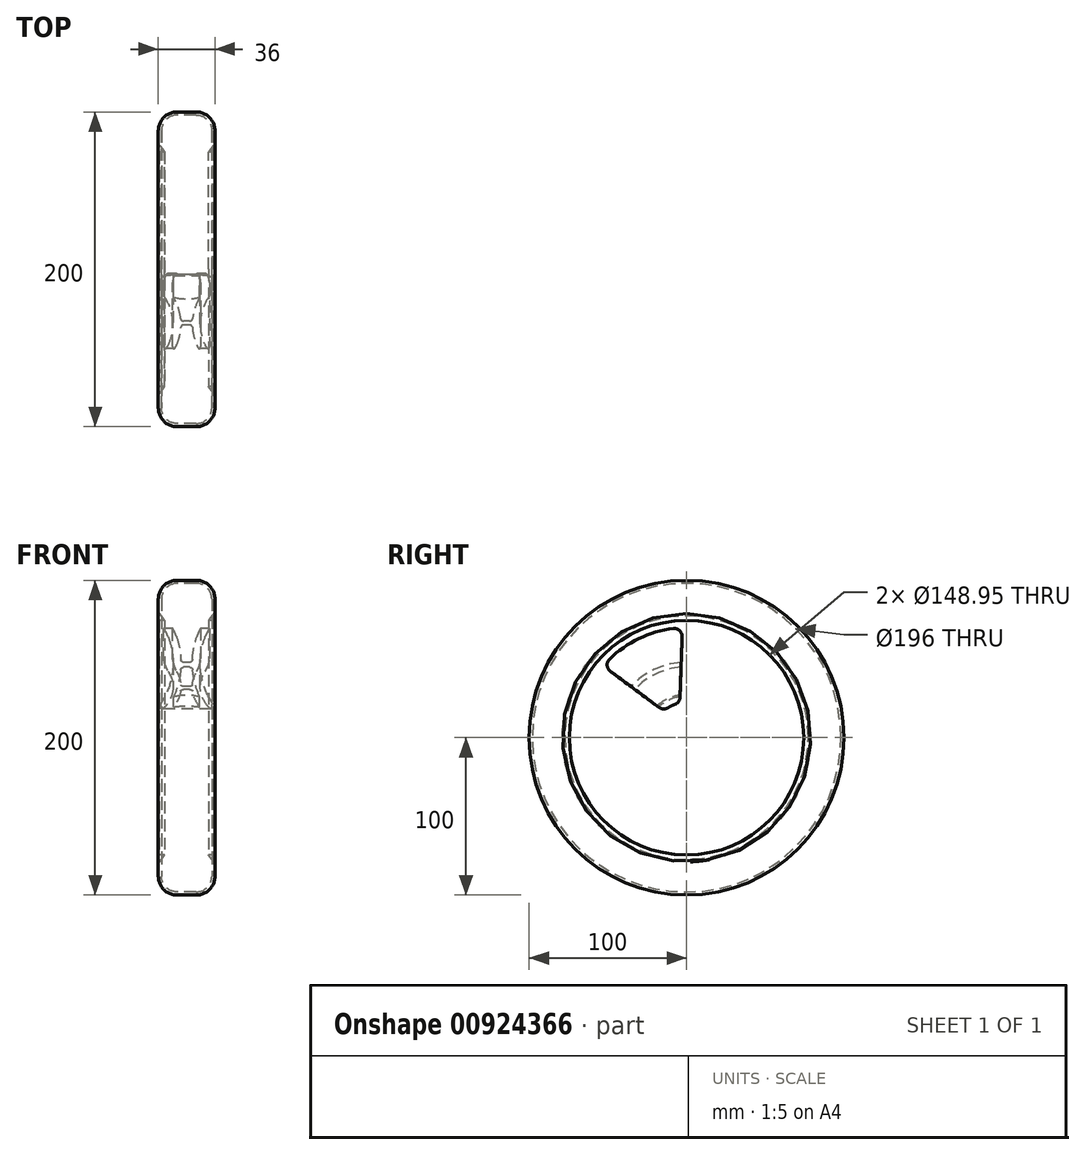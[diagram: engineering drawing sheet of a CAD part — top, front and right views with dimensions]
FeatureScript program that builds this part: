
annotation { "Feature Type Name" : "Feature", "Feature Type Description" : "" }
export const myFeature = defineFeature(function(context is Context, id is Id, definition is map)
    precondition{}
    {
        {
            var Q0;
            Q0=qCreatedBy(makeId("Front.planeOp"),FACE);
            var sketch = newSketch(context, id + "F0", { "sketchPlane" : qUnion([Q0])});
            skLineSegment(sketch, "E0", {"start": v(0, 0) * mm, "end": v(0, 100) * mm, "construction": true});
            skLineSegment(sketch, "E1", {"start": v(0, 10) * mm, "end": v(-18, 10) * mm});
            skLineSegment(sketch, "E2", {"start": v(-18, 10) * mm, "end": v(-18, 16.78) * mm});
            skLineSegment(sketch, "E3", {"start": v(0, 100) * mm, "end": v(-6, 100) * mm});
            skLineSegment(sketch, "E4", {"start": v(-18, 88) * mm, "end": v(-18, 79.22) * mm});
            skArc(sketch, "E5", {"start": v(-16.3, 22.36) * mm, "mid": v(-8.63, 48.63) * mm, "end": v(-17.6, 74.48) * mm});
            skArc(sketch, "E6.0", {"start": v(-13.48, 73.83) * mm, "mid": v(-15.23, 76.3) * mm, "end": v(-17.12, 78.67) * mm});
            skPoint(sketch, "E7.orphan", {"position": v(0, 75) * mm});
            skArc(sketch, "E8.MirrorCS", {"start": v(13.48, 73.83) * mm, "mid": v(15.23, 76.3) * mm, "end": v(17.12, 78.67) * mm});
            skArc(sketch, "E9.MirrorCS", {"start": v(16.3, 22.36) * mm, "mid": v(8.63, 48.63) * mm, "end": v(17.6, 74.48) * mm});
            skLineSegment(sketch, "E10.MirrorCS", {"start": v(18, 78.35) * mm, "end": v(18, 75.67) * mm});
            skLineSegment(sketch, "E11.MirrorCS", {"start": v(0, 100) * mm, "end": v(6, 100) * mm});
            skLineSegment(sketch, "E12.MirrorCS", {"start": v(0, 10) * mm, "end": v(18, 10) * mm});
            skLineSegment(sketch, "E13.MirrorCS", {"start": v(18, 10) * mm, "end": v(18, 16.78) * mm});
            skArc(sketch, "E14", {"start": v(-13.48, 73.83) * mm, "mid": v(0, 72.36) * mm, "end": v(13.48, 73.83) * mm});
            skPoint(sketch, "E15.orphan", {"position": v(-14.28, 20) * mm});
            skPoint(sketch, "E16.orphan", {"position": v(14.28, 20) * mm});
            skPoint(sketch, "E17.visualSharp", {"position": v(-18, 100) * mm});
            skArc(sketch, "E17.filletArc", {"start": v(-6, 100) * mm, "mid": v(-14.49, 96.49) * mm, "end": v(-18, 88) * mm});
            skArc(sketch, "E18.MirrorCS", {"start": v(6, 100) * mm, "mid": v(14.49, 96.49) * mm, "end": v(18, 88) * mm});
            skPoint(sketch, "E19.orphan", {"position": v(18, 100) * mm});
            skLineSegment(sketch, "E20", {"start": v(-18, 78.35) * mm, "end": v(-18, 75.67) * mm});
            skPoint(sketch, "E21.visualSharp", {"position": v(-18, 79.68) * mm});
            skArc(sketch, "E21.filletArc", {"start": v(-17.12, 78.67) * mm, "mid": v(-17.67, 78.82) * mm, "end": v(-18, 78.35) * mm});
            skPoint(sketch, "E22.newPointA", {"position": v(18, 79.68) * mm});
            skArc(sketch, "E22.filletArc", {"start": v(18, 78.35) * mm, "mid": v(17.67, 78.82) * mm, "end": v(17.12, 78.67) * mm});
            skLineSegment(sketch, "E23.MirrorCS", {"start": v(18, 88) * mm, "end": v(18, 79.22) * mm});
            skPoint(sketch, "E24.1.start.orphan", {"position": v(-6, 97) * mm});
            skPoint(sketch, "E25.0.start.orphan", {"position": v(0, 97) * mm});
            skPoint(sketch, "E26.MirrorCS.end.orphan", {"position": v(6, 97) * mm});
            skPoint(sketch, "E27.MirrorCS.end.orphan", {"position": v(15, 88) * mm});
            skPoint(sketch, "E28.MirrorCS.end.orphan", {"position": v(15, 80.8) * mm});
            skPoint(sketch, "E29.MirrorCS.start.orphan", {"position": v(9.5, 73.08) * mm});
            skPoint(sketch, "E30.0.start.orphan", {"position": v(-9.5, 73.08) * mm});
            skPoint(sketch, "E24.0.end.orphan", {"position": v(-15, 80.8) * mm});
            skPoint(sketch, "E24.0.start.orphan", {"position": v(-15, 88) * mm});
            skPoint(sketch, "E31.visualSharp", {"position": v(-18, 75) * mm});
            skArc(sketch, "E31.filletArc", {"start": v(-18, 75.67) * mm, "mid": v(-17.9, 75.04) * mm, "end": v(-17.6, 74.48) * mm});
            skPoint(sketch, "E32.visualSharp", {"position": v(18, 75) * mm});
            skArc(sketch, "E32.filletArc", {"start": v(17.6, 74.48) * mm, "mid": v(17.9, 75.04) * mm, "end": v(18, 75.67) * mm});
            skLineSegment(sketch, "E33.0", {"start": v(-16, 88) * mm, "end": v(-16, 77.31) * mm});
            skArc(sketch, "E33.1", {"start": v(-6, 98) * mm, "mid": v(-13.07, 95.07) * mm, "end": v(-16, 88) * mm});
            skLineSegment(sketch, "E33.2", {"start": v(16, 88) * mm, "end": v(16, 77.31) * mm});
            skArc(sketch, "E33.3", {"start": v(6, 98) * mm, "mid": v(13.07, 95.07) * mm, "end": v(16, 88) * mm});
            skLineSegment(sketch, "E33.4", {"start": v(0, 98) * mm, "end": v(6, 98) * mm});
            skLineSegment(sketch, "E33.5", {"start": v(0, 98) * mm, "end": v(-6, 98) * mm});
            skPoint(sketch, "E34.visualSharp", {"position": v(-18, 78.35) * mm});
            skArc(sketch, "E34.filletArc", {"start": v(-18, 79.22) * mm, "mid": v(-17.87, 78.93) * mm, "end": v(-17.57, 78.84) * mm});
            skArc(sketch, "E35.MirrorCS", {"start": v(18, 79.22) * mm, "mid": v(17.87, 78.93) * mm, "end": v(17.57, 78.84) * mm});
            skPoint(sketch, "E36.visualSharp", {"position": v(-18, 20) * mm});
            skArc(sketch, "E36.filletArc", {"start": v(-16.3, 22.36) * mm, "mid": v(-17.56, 19.7) * mm, "end": v(-18, 16.78) * mm});
            skPoint(sketch, "E37.visualSharp", {"position": v(18, 20) * mm});
            skArc(sketch, "E37.filletArc", {"start": v(18, 16.78) * mm, "mid": v(17.56, 19.7) * mm, "end": v(16.3, 22.36) * mm});
            skLineSegment(sketch, "E38", {"start": v(0, 0) * mm, "end": v(25.5, 0) * mm, "construction": true});
            skArc(sketch, "E39", {"start": v(8.32, 26.33) * mm, "mid": v(0, 27.6) * mm, "end": v(-8.32, 26.33) * mm});
            skArc(sketch, "E40.0", {"start": v(-8.32, 26.33) * mm, "mid": v(-5.33, 34.52) * mm, "end": v(-3.81, 43.1) * mm});
            skArc(sketch, "E40.2", {"start": v(8.32, 26.33) * mm, "mid": v(5.33, 34.52) * mm, "end": v(3.81, 43.1) * mm});
            skLineSegment(sketch, "E41", {"start": v(-3.63, 46.43) * mm, "end": v(3.63, 46.43) * mm, "construction": true});
            skLineSegment(sketch, "E42", {"start": v(-1.68, 47.93) * mm, "end": v(1.68, 47.93) * mm});
            skLineSegment(sketch, "E43.MirrorCS", {"start": v(-1.82, 44.93) * mm, "end": v(1.82, 44.93) * mm});
            skPoint(sketch, "E44.orphan", {"position": v(3.62, 44.93) * mm});
            skPoint(sketch, "E45.orphan", {"position": v(-3.62, 44.93) * mm});
            skArc(sketch, "E46.trimOffspring", {"start": v(3.67, 49.84) * mm, "mid": v(5.41, 60.78) * mm, "end": v(9.52, 71.06) * mm});
            skArc(sketch, "E47.trimOffspring", {"start": v(-3.67, 49.84) * mm, "mid": v(-5.41, 60.78) * mm, "end": v(-9.52, 71.06) * mm});
            skPoint(sketch, "E48.visualSharp", {"position": v(-3.62, 47.93) * mm});
            skArc(sketch, "E48.filletArc", {"start": v(-3.67, 49.84) * mm, "mid": v(-3.06, 48.49) * mm, "end": v(-1.68, 47.93) * mm});
            skPoint(sketch, "E49.visualSharp", {"position": v(3.62, 47.93) * mm});
            skArc(sketch, "E49.filletArc", {"start": v(1.68, 47.93) * mm, "mid": v(3.06, 48.49) * mm, "end": v(3.67, 49.84) * mm});
            skPoint(sketch, "E50.visualSharp", {"position": v(-3.69, 44.93) * mm});
            skArc(sketch, "E50.filletArc", {"start": v(-1.82, 44.93) * mm, "mid": v(-3.17, 44.4) * mm, "end": v(-3.81, 43.1) * mm});
            skPoint(sketch, "E51.visualSharp", {"position": v(3.69, 44.93) * mm});
            skArc(sketch, "E51.filletArc", {"start": v(3.81, 43.1) * mm, "mid": v(3.17, 44.4) * mm, "end": v(1.82, 44.93) * mm});
            skArc(sketch, "E52.0", {"start": v(-9.52, 71.06) * mm, "mid": v(0, 70.36) * mm, "end": v(9.52, 71.06) * mm});
            skSolve(sketch);
        }
        {
            var Q0;
            Q0=makeQuery(id+"F0.imprint","IMPRINT",FACE,{"disambiguationData":[TD([[makeQuery(id+"F0.imprint","IMPRINT",EDGE,{"derivedFrom":sQuery(id+"F0.wireOp",EDGE,"E1")}),-1.0]])]});
            var Q1;
            Q1=sQuery(id+"F0.wireOp",EDGE,"E38");
            revolve(context, id + "F1", {"surfaceOperationType" : NewSurfaceOperationType.NEW, "entities" : qUnion([Q0]), "axis" : qUnion([Q1]), "revolveType" : RevolveType.FULL});
        }
        {
            var Q0;
            Q0=makeQuery(id+"F0.imprint","IMPRINT",FACE,{"disambiguationData":[TD([[makeQuery(id+"F0.imprint","IMPRINT",EDGE,{"derivedFrom":sQuery(id+"F0.wireOp",EDGE,"E3")}),1.0]])]});
            var Q1;
            Q1=sQuery(id+"F0.wireOp",EDGE,"E38");
            revolve(context, id + "F2", {"surfaceOperationType" : NewSurfaceOperationType.NEW, "entities" : qUnion([Q0]), "axis" : qUnion([Q1]), "revolveType" : RevolveType.FULL});
        }
        {
            var Q0;
            Q0=qCreatedBy(makeId("Right.planeOp"),FACE);
            var sketch = newSketch(context, id + "F3", { "sketchPlane" : qUnion([Q0])});
            skArc(sketch, "E53.0", {"start": v(-11.82, 18.99) * mm, "mid": v(-9.7, 20.15) * mm, "end": v(-7.48, 21.08) * mm});
            skCircle(sketch, "E54.0", {"center": v(0, 0) * mm, "radius": 74.48 * mm});
            skPoint(sketch, "E55.0", {"position": v(0, 72.36) * mm});
            skLineSegment(sketch, "E56", {"start": v(0, 69.82) * mm, "end": v(0, 22.36) * mm, "construction": true});
            skArc(sketch, "E57", {"start": v(48.95, 49.79) * mm, "mid": v(30.3, 62.9) * mm, "end": v(8.4, 69.31) * mm});
            skLineSegment(sketch, "E58", {"start": v(2.8, 64.17) * mm, "end": v(4.15, 25.61) * mm});
            skLineSegment(sketch, "E59.MirrorCS", {"start": v(-2.8, 64.17) * mm, "end": v(-4.15, 25.61) * mm});
            skLineSegment(sketch, "E60.1.0", {"start": v(-51.92, 37.82) * mm, "end": v(-22.62, 12.72) * mm});
            skLineSegment(sketch, "E60.1.1", {"start": v(-48.42, 42.2) * mm, "end": v(-17.44, 19.22) * mm});
            skLineSegment(sketch, "E60.2.0", {"start": v(-61.94, -17.02) * mm, "end": v(-24.05, -9.75) * mm});
            skLineSegment(sketch, "E60.2.1", {"start": v(-63.19, -11.54) * mm, "end": v(-25.9, -1.65) * mm});
            skLineSegment(sketch, "E60.3.0", {"start": v(-25.31, -59.04) * mm, "end": v(-7.37, -24.88) * mm});
            skLineSegment(sketch, "E60.3.1", {"start": v(-30.37, -56.6) * mm, "end": v(-14.86, -21.28) * mm});
            skLineSegment(sketch, "E60.4.0", {"start": v(30.37, -56.6) * mm, "end": v(14.86, -21.28) * mm});
            skLineSegment(sketch, "E60.4.1", {"start": v(25.31, -59.04) * mm, "end": v(7.37, -24.88) * mm});
            skLineSegment(sketch, "E60.5.0", {"start": v(63.19, -11.54) * mm, "end": v(25.9, -1.65) * mm});
            skLineSegment(sketch, "E60.5.1", {"start": v(61.94, -17.02) * mm, "end": v(24.05, -9.75) * mm});
            skLineSegment(sketch, "E60.6.0", {"start": v(48.42, 42.2) * mm, "end": v(17.44, 19.22) * mm});
            skLineSegment(sketch, "E60.6.1", {"start": v(51.92, 37.82) * mm, "end": v(22.62, 12.72) * mm});
            skArc(sketch, "E61.trimOffspring", {"start": v(-8.4, 69.31) * mm, "mid": v(-30.3, 62.9) * mm, "end": v(-48.95, 49.79) * mm});
            skArc(sketch, "E62.trimOffspring", {"start": v(-59.43, 36.64) * mm, "mid": v(-68.07, 15.54) * mm, "end": v(-69.44, -7.23) * mm});
            skArc(sketch, "E63.trimOffspring", {"start": v(7.48, 21.08) * mm, "mid": v(9.7, 20.15) * mm, "end": v(11.82, 18.99) * mm});
            skArc(sketch, "E64.trimOffspring", {"start": v(18.88, -11.98) * mm, "mid": v(17.48, -13.94) * mm, "end": v(15.88, -15.74) * mm});
            skArc(sketch, "E65.trimOffspring", {"start": v(-15.88, -15.74) * mm, "mid": v(-17.48, -13.94) * mm, "end": v(-18.88, -11.98) * mm});
            skArc(sketch, "E66.trimOffspring", {"start": v(2.4, -22.23) * mm, "mid": v(0, -22.36) * mm, "end": v(-2.4, -22.23) * mm});
            skArc(sketch, "E67.trimOffspring", {"start": v(-22.21, 2.6) * mm, "mid": v(-21.8, 4.98) * mm, "end": v(-21.14, 7.3) * mm});
            skArc(sketch, "E68.trimOffspring", {"start": v(-22.5, -66.1) * mm, "mid": v(0, -69.82) * mm, "end": v(22.5, -66.1) * mm});
            skArc(sketch, "E69.trimOffspring", {"start": v(37.65, -58.8) * mm, "mid": v(54.59, -43.53) * mm, "end": v(65.7, -23.62) * mm});
            skArc(sketch, "E70.trimOffspring", {"start": v(69.44, -7.23) * mm, "mid": v(68.07, 15.54) * mm, "end": v(59.43, 36.64) * mm});
            skArc(sketch, "E71.MirrorCS", {"start": v(22.21, 2.6) * mm, "mid": v(21.8, 4.98) * mm, "end": v(21.14, 7.3) * mm});
            skPoint(sketch, "E72.visualSharp", {"position": v(-52.92, 45.54) * mm});
            skArc(sketch, "E72.filletArc", {"start": v(-48.95, 49.79) * mm, "mid": v(-50.43, 45.87) * mm, "end": v(-48.42, 42.2) * mm});
            skArc(sketch, "E73.trimOffspring", {"start": v(-65.7, -23.62) * mm, "mid": v(-54.59, -43.53) * mm, "end": v(-37.65, -58.8) * mm});
            skPoint(sketch, "E74.visualSharp", {"position": v(-2.61, 69.77) * mm});
            skArc(sketch, "E74.filletArc", {"start": v(-2.8, 64.17) * mm, "mid": v(-4.42, 68.03) * mm, "end": v(-8.4, 69.31) * mm});
            skPoint(sketch, "E75.visualSharp", {"position": v(2.61, 69.77) * mm});
            skArc(sketch, "E75.filletArc", {"start": v(8.4, 69.31) * mm, "mid": v(4.42, 68.03) * mm, "end": v(2.8, 64.17) * mm});
            skPoint(sketch, "E76.visualSharp", {"position": v(52.92, 45.54) * mm});
            skArc(sketch, "E76.filletArc", {"start": v(48.42, 42.2) * mm, "mid": v(50.43, 45.87) * mm, "end": v(48.95, 49.79) * mm});
            skPoint(sketch, "E77.visualSharp", {"position": v(67.44, -18.07) * mm});
            skArc(sketch, "E77.filletArc", {"start": v(65.7, -23.62) * mm, "mid": v(65.34, -19.45) * mm, "end": v(61.94, -17.02) * mm});
            skPoint(sketch, "E78.visualSharp", {"position": v(32.62, -61.73) * mm});
            skArc(sketch, "E78.filletArc", {"start": v(30.37, -56.6) * mm, "mid": v(33.5, -59.38) * mm, "end": v(37.65, -58.8) * mm});
            skPoint(sketch, "E79.visualSharp", {"position": v(-27.92, -64) * mm});
            skArc(sketch, "E79.filletArc", {"start": v(-25.31, -59.04) * mm, "mid": v(-25.53, -63.21) * mm, "end": v(-22.5, -66.1) * mm});
            skPoint(sketch, "E80.visualSharp", {"position": v(-67.44, -18.07) * mm});
            skArc(sketch, "E80.filletArc", {"start": v(-61.94, -17.02) * mm, "mid": v(-65.34, -19.45) * mm, "end": v(-65.7, -23.62) * mm});
            skPoint(sketch, "E81.visualSharp", {"position": v(-56.18, 41.46) * mm});
            skArc(sketch, "E81.filletArc", {"start": v(-51.92, 37.82) * mm, "mid": v(-55.95, 38.96) * mm, "end": v(-59.43, 36.64) * mm});
            skPoint(sketch, "E82.visualSharp", {"position": v(-68.6, -12.98) * mm});
            skArc(sketch, "E82.filletArc", {"start": v(-69.44, -7.23) * mm, "mid": v(-67.3, -10.83) * mm, "end": v(-63.19, -11.54) * mm});
            skPoint(sketch, "E83.visualSharp", {"position": v(-32.62, -61.73) * mm});
            skArc(sketch, "E83.filletArc", {"start": v(-37.65, -58.8) * mm, "mid": v(-33.5, -59.38) * mm, "end": v(-30.37, -56.6) * mm});
            skPoint(sketch, "E84.visualSharp", {"position": v(27.92, -64) * mm});
            skArc(sketch, "E84.filletArc", {"start": v(22.5, -66.1) * mm, "mid": v(25.53, -63.21) * mm, "end": v(25.31, -59.04) * mm});
            skPoint(sketch, "E85.visualSharp", {"position": v(68.6, -12.98) * mm});
            skArc(sketch, "E85.filletArc", {"start": v(63.19, -11.54) * mm, "mid": v(67.3, -10.83) * mm, "end": v(69.44, -7.23) * mm});
            skPoint(sketch, "E86.visualSharp", {"position": v(56.18, 41.46) * mm});
            skArc(sketch, "E86.filletArc", {"start": v(59.43, 36.64) * mm, "mid": v(55.95, 38.96) * mm, "end": v(51.92, 37.82) * mm});
            skPoint(sketch, "E87.visualSharp", {"position": v(-14.5, 17.03) * mm});
            skArc(sketch, "E87.filletArc", {"start": v(-17.44, 19.22) * mm, "mid": v(-14.66, 18.24) * mm, "end": v(-11.82, 18.99) * mm});
            skPoint(sketch, "E88.visualSharp", {"position": v(-4.28, 21.95) * mm});
            skArc(sketch, "E88.filletArc", {"start": v(-7.48, 21.08) * mm, "mid": v(-5.12, 22.83) * mm, "end": v(-4.15, 25.61) * mm});
            skPoint(sketch, "E89.visualSharp", {"position": v(14.5, 17.03) * mm});
            skArc(sketch, "E89.filletArc", {"start": v(11.82, 18.99) * mm, "mid": v(14.66, 18.24) * mm, "end": v(17.44, 19.22) * mm});
            skPoint(sketch, "E90.visualSharp", {"position": v(22.35, -0.71) * mm});
            skArc(sketch, "E90.filletArc", {"start": v(22.21, 2.6) * mm, "mid": v(23.4, -0.1) * mm, "end": v(25.9, -1.65) * mm});
            skPoint(sketch, "E91.visualSharp", {"position": v(13.38, -17.92) * mm});
            skArc(sketch, "E91.filletArc", {"start": v(15.88, -15.74) * mm, "mid": v(14.52, -18.35) * mm, "end": v(14.86, -21.28) * mm});
            skPoint(sketch, "E92.visualSharp", {"position": v(-5.67, -21.63) * mm});
            skArc(sketch, "E92.filletArc", {"start": v(-2.4, -22.23) * mm, "mid": v(-5.3, -22.8) * mm, "end": v(-7.37, -24.88) * mm});
            skPoint(sketch, "E93.visualSharp", {"position": v(-20.45, -9.06) * mm});
            skArc(sketch, "E93.filletArc", {"start": v(-18.88, -11.98) * mm, "mid": v(-21.12, -10.07) * mm, "end": v(-24.05, -9.75) * mm});
            skPoint(sketch, "E94.visualSharp", {"position": v(-19.83, 10.34) * mm});
            skArc(sketch, "E94.filletArc", {"start": v(-21.14, 7.3) * mm, "mid": v(-21.04, 10.24) * mm, "end": v(-22.62, 12.72) * mm});
            skPoint(sketch, "E95.visualSharp", {"position": v(-22.35, -0.71) * mm});
            skArc(sketch, "E95.filletArc", {"start": v(-25.9, -1.65) * mm, "mid": v(-23.4, -0.1) * mm, "end": v(-22.21, 2.6) * mm});
            skPoint(sketch, "E96.visualSharp", {"position": v(-13.38, -17.92) * mm});
            skArc(sketch, "E96.filletArc", {"start": v(-14.86, -21.28) * mm, "mid": v(-14.52, -18.35) * mm, "end": v(-15.88, -15.74) * mm});
            skPoint(sketch, "E97.visualSharp", {"position": v(5.67, -21.63) * mm});
            skArc(sketch, "E97.filletArc", {"start": v(7.37, -24.88) * mm, "mid": v(5.3, -22.8) * mm, "end": v(2.4, -22.23) * mm});
            skPoint(sketch, "E98.visualSharp", {"position": v(19.83, 10.34) * mm});
            skArc(sketch, "E98.filletArc", {"start": v(22.62, 12.72) * mm, "mid": v(21.04, 10.24) * mm, "end": v(21.14, 7.3) * mm});
            skPoint(sketch, "E99.visualSharp", {"position": v(4.28, 21.95) * mm});
            skArc(sketch, "E99.filletArc", {"start": v(4.15, 25.61) * mm, "mid": v(5.12, 22.83) * mm, "end": v(7.48, 21.08) * mm});
            skPoint(sketch, "E100.visualSharp", {"position": v(20.45, -9.06) * mm});
            skArc(sketch, "E100.filletArc", {"start": v(24.05, -9.75) * mm, "mid": v(21.12, -10.07) * mm, "end": v(18.88, -11.98) * mm});
            skSolve(sketch);
        }
        {
            var Q0;
            Q0=makeQuery(id+"F3.imprint","IMPRINT",FACE,{"disambiguationData":[TD([[makeQuery(id+"F3.imprint","IMPRINT",EDGE,{"derivedFrom":sQuery(id+"F3.wireOp",EDGE,"E57")}),1.0]])]});
            var Q1;
            Q1=makeQuery(id+"F3.imprint","IMPRINT",FACE,{"disambiguationData":[TD([[makeQuery(id+"F3.imprint","IMPRINT",EDGE,{"derivedFrom":sQuery(id+"F3.wireOp",EDGE,"E53.0")}),1.0]])]});
            var Q2;
            Q2=makeQuery(id+"F3.imprint","IMPRINT",FACE,{"disambiguationData":[TD([[makeQuery(id+"F3.imprint","IMPRINT",EDGE,{"derivedFrom":sQuery(id+"F3.wireOp",EDGE,"E60.5.0")}),-1.0]])]});
            var Q3;
            Q3=makeQuery(id+"F3.imprint","IMPRINT",FACE,{"disambiguationData":[TD([[makeQuery(id+"F3.imprint","IMPRINT",EDGE,{"derivedFrom":sQuery(id+"F3.wireOp",EDGE,"E60.4.0")}),-1.0]])]});
            var Q4;
            Q4=makeQuery(id+"F3.imprint","IMPRINT",FACE,{"disambiguationData":[TD([[makeQuery(id+"F3.imprint","IMPRINT",EDGE,{"derivedFrom":sQuery(id+"F3.wireOp",EDGE,"E60.3.0")}),-1.0]])]});
            var Q5;
            {var subQ0=sQuery(id+"F3.wireOp",EDGE,"E60.2.0");Q5=makeQuery(id+"F3.imprint","IMPRINT",FACE,{"disambiguationData":[TD([[makeQuery(id+"F3.imprint","IMPRINT",EDGE,{"derivedFrom":subQ0}),-1.0]])]});}
            var Q6;
            {var subQ0=sQuery(id+"F3.wireOp",EDGE,"E60.1.0");Q6=makeQuery(id+"F3.imprint","IMPRINT",FACE,{"disambiguationData":[TD([[makeQuery(id+"F3.imprint","IMPRINT",EDGE,{"derivedFrom":subQ0}),-1.0]])]});}
            extrude(context, id + "F4", {"entities" : qUnion([Q0, Q1, Q2, Q3, Q4, Q5, Q6]), "operationType" : NewBodyOperationType.REMOVE, "endBound" : BoundingType.SYMMETRIC, "depth" : 100 * mm, "offsetDistance" : 25 * mm});
        }
    });
